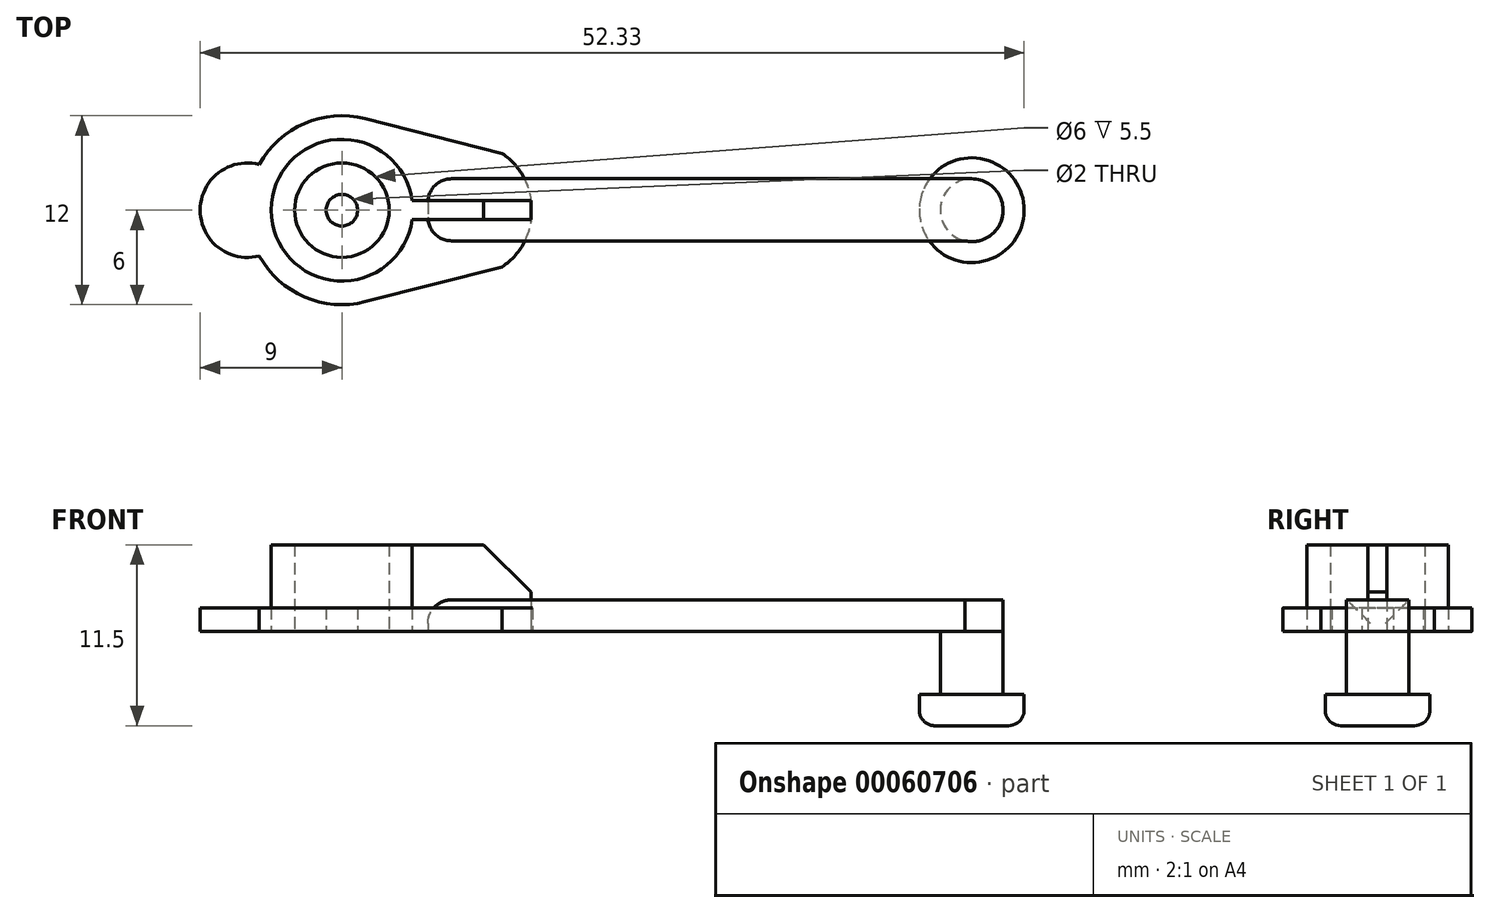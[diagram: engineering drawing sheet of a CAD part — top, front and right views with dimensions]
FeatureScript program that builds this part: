
annotation { "Feature Type Name" : "Feature", "Feature Type Description" : "" }
export const myFeature = defineFeature(function(context is Context, id is Id, definition is map)
    precondition{}
    {
        {
            var Q0;
            Q0=qCreatedBy(makeId("Top.planeOp"),FACE);
            var sketch = newSketch(context, id + "F0", { "sketchPlane" : qUnion([Q0])});
            skCircle(sketch, "E0", {"center": v(0, 0) * mm, "radius": 3 * mm});
            skArc(sketch, "E1", {"start": v(4.46, 0.6) * mm, "mid": v(-4.5, 0) * mm, "end": v(4.46, -0.6) * mm});
            skLineSegment(sketch, "E2.rect.bottom", {"start": v(12, -0.6) * mm, "end": v(4.46, -0.6) * mm});
            skLineSegment(sketch, "E2.rect.top", {"start": v(12, 0.6) * mm, "end": v(4.46, 0.6) * mm});
            skLineSegment(sketch, "E2.rect.left", {"start": v(12, -0.6) * mm, "end": v(12, 0.6) * mm});
            skPoint(sketch, "E2.rect.middle", {"position": v(7.75, 0) * mm});
            skArc(sketch, "E3", {"start": v(1.48, 5.81) * mm, "mid": v(-2.38, 5.5) * mm, "end": v(-5.25, 2.9) * mm});
            skArc(sketch, "E4", {"start": v(10.18, -3.6) * mm, "mid": v(12.1, 0) * mm, "end": v(10.18, 3.6) * mm});
            skLineSegment(sketch, "E5", {"start": v(7.33, -4.32) * mm, "end": v(1.48, -5.81) * mm});
            skLineSegment(sketch, "E6", {"start": v(7.33, 4.32) * mm, "end": v(1.48, 5.81) * mm});
            skPoint(sketch, "E7.orphan", {"position": v(10.18, 3.6) * mm});
            skPoint(sketch, "E8.orphan", {"position": v(10.18, -3.6) * mm});
            skLineSegment(sketch, "E9", {"start": v(7.33, 4.32) * mm, "end": v(10.18, 3.6) * mm});
            skLineSegment(sketch, "E10", {"start": v(10.18, -3.6) * mm, "end": v(7.33, -4.32) * mm});
            skCircle(sketch, "E11", {"center": v(0, 0) * mm, "radius": 1 * mm});
            skArc(sketch, "E12", {"start": v(-5.25, 2.9) * mm, "mid": v(-9, 0) * mm, "end": v(-5.25, -2.9) * mm});
            skArc(sketch, "E13.trimOffspring", {"start": v(-5.25, -2.9) * mm, "mid": v(-2.38, -5.5) * mm, "end": v(1.48, -5.81) * mm});
            skSolve(sketch);
        }
        {
            var Q0;
            {var subQ2=sQuery(id+"F0.wireOp",EDGE,"E1");Q0=makeQuery(id+"F0.imprint","IMPRINT",FACE,{"disambiguationData":[TD([[makeQuery(id+"F0.imprint","IMPRINT",EDGE,{"derivedFrom":subQ2}),-1.0]])]});}
            var Q1;
            Q1=makeQuery(id+"F0.imprint","IMPRINT",FACE,{"disambiguationData":[TD([[makeQuery(id+"F0.imprint","IMPRINT",EDGE,{"derivedFrom":sQuery(id+"F0.wireOp",EDGE,"E0")}),-1.0]])]});
            var Q2;
            {var subQ1=sQuery(id+"F0.wireOp",EDGE,"E2.rect.bottom");Q2=makeQuery(id+"F0.imprint","IMPRINT",FACE,{"disambiguationData":[TD([[makeQuery(id+"F0.imprint","IMPRINT",EDGE,{"derivedFrom":subQ1}),-1.0]])]});}
            var Q3;
            Q3=makeQuery(id+"F0.imprint","IMPRINT",FACE,{"disambiguationData":[TD([[makeQuery(id+"F0.imprint","IMPRINT",EDGE,{"derivedFrom":sQuery(id+"F0.wireOp",EDGE,"E0")}),1.0]])]});
            extrude(context, id + "F1", {"entities" : qUnion([Q0, Q1, Q2, Q3]), "depth" : 1.5 * mm});
        }
        {
            var Q0;
            Q0=makeQuery(id+"F0.imprint","IMPRINT",FACE,{"disambiguationData":[TD([[makeQuery(id+"F0.imprint","IMPRINT",EDGE,{"derivedFrom":sQuery(id+"F0.wireOp",EDGE,"E0")}),-1.0]])]});
            var Q1;
            {var subQ1=sQuery(id+"F0.wireOp",EDGE,"E2.rect.bottom");Q1=makeQuery(id+"F0.imprint","IMPRINT",FACE,{"disambiguationData":[TD([[makeQuery(id+"F0.imprint","IMPRINT",EDGE,{"derivedFrom":subQ1}),-1.0]])]});}
            extrude(context, id + "F2", {"entities" : qUnion([Q0, Q1]), "depth" : 5.5 * mm});
        }
        {
            var Q0;
            Q0=makeQuery(id+"F2.opExtrude","CAP_EDGE",EDGE,{"disambiguationData":[OSD([sQuery(id+"F0.wireOp",EDGE,"E2.rect.left")])],"isStart":false});
            chamfer(context, id + "F3", {"entities" : qUnion([Q0]), "chamferType" : ChamferType.OFFSET_ANGLE, "width" : 3 * mm, "oppositeDirection" : false, "angle" : 45 * degree});
        }
        {
            var Q0;
            {var subQ2=sQuery(id+"F0.wireOp",EDGE,"E1");Q0=makeQuery(id+"F0.imprint","IMPRINT",FACE,{"disambiguationData":[TD([[makeQuery(id+"F0.imprint","IMPRINT",EDGE,{"derivedFrom":subQ2}),-1.0]])]});}
            var sketch = newSketch(context, id + "F4", { "sketchPlane" : qUnion([Q0])});
            skCircle(sketch, "E14", {"center": v(40, 0) * mm, "radius": 2 * mm});
            skLineSegment(sketch, "E15.bottom", {"start": v(40, 2) * mm, "end": v(5.46, 2) * mm});
            skLineSegment(sketch, "E15.top", {"start": v(40, -1.95) * mm, "end": v(5.46, -1.95) * mm});
            skLineSegment(sketch, "E15.left", {"start": v(40, 2) * mm, "end": v(40, -1.95) * mm});
            skLineSegment(sketch, "E15.right", {"start": v(5.46, 2) * mm, "end": v(5.46, -1.95) * mm});
            skSolve(sketch);
        }
        {
            var Q0;
            {var subQ0=sQuery(id+"F4.wireOp",EDGE,"E15.left");Q0=makeQuery(id+"F4.imprint","IMPRINT",FACE,{"disambiguationData":[TD([[makeQuery(id+"F4.imprint","IMPRINT",EDGE,{"derivedFrom":subQ0}),1.0]])]});}
            var Q1;
            {var subQ0=sQuery(id+"F4.wireOp",EDGE,"E15.left");Q1=makeQuery(id+"F4.imprint","IMPRINT",FACE,{"disambiguationData":[TD([[makeQuery(id+"F4.imprint","IMPRINT",EDGE,{"derivedFrom":subQ0}),-1.0]])]});}
            extrude(context, id + "F5", {"entities" : qUnion([Q0, Q1]), "oppositeDirection" : true, "depth" : 4 * mm});
        }
        {
            var Q0;
            {var subQ1=sQuery(id+"F4.wireOp",EDGE,"E14");var subQ3=sQuery(id+"F4.wireOp",EDGE,"E15.top");var subQ4=makeQuery(id+"F4.imprint","INTERSECT",VERTEX,{"derivedFrom":[subQ1,subQ3]});Q0=makeQuery(id+"F4.imprint","IMPRINT",FACE,{"disambiguationData":[TD([[makeQuery(id+"F4.imprint","IMPRINT",EDGE,{"disambiguationData":[TD([[subQ4,-1.0]])],"derivedFrom":subQ3}),-1.0]])]});}
            var Q1;
            {var subQ5=makeQuery(id+"F0.imprint","IMPRINT",EDGE,{"derivedFrom":sQuery(id+"F0.wireOp",EDGE,"E2.rect.left")});Q1=makeQuery(id+"F4.imprint","IMPRINT",FACE,{"disambiguationData":[TD([[makeQuery(id+"F4.imprint","IMPRINT",EDGE,{"derivedFrom":subQ5}),1.0]])]});}
            var Q2;
            {var subQ5=makeQuery(id+"F0.imprint","IMPRINT",EDGE,{"derivedFrom":sQuery(id+"F0.wireOp",EDGE,"E2.rect.left")});Q2=makeQuery(id+"F4.imprint","IMPRINT",FACE,{"disambiguationData":[TD([[makeQuery(id+"F4.imprint","IMPRINT",EDGE,{"derivedFrom":subQ5}),-1.0]])]});}
            var Q3;
            {var subQ0=sQuery(id+"F4.wireOp",EDGE,"E15.left");Q3=makeQuery(id+"F4.imprint","IMPRINT",FACE,{"disambiguationData":[TD([[makeQuery(id+"F4.imprint","IMPRINT",EDGE,{"derivedFrom":subQ0}),-1.0]])]});}
            var Q4;
            {var subQ0=sQuery(id+"F4.wireOp",EDGE,"E15.left");Q4=makeQuery(id+"F4.imprint","IMPRINT",FACE,{"disambiguationData":[TD([[makeQuery(id+"F4.imprint","IMPRINT",EDGE,{"derivedFrom":subQ0}),1.0]])]});}
            extrude(context, id + "F6", {"entities" : qUnion([Q0, Q1, Q2, Q3, Q4]), "depth" : 2 * mm});
        }
        {
            var Q0;
            Q0=makeQuery(id+"F6.opExtrude","CAP_EDGE",EDGE,{"disambiguationData":[OSD([sQuery(id+"F4.wireOp",EDGE,"E15.right")])],"isStart":false});
            var Q1;
            Q1=makeQuery(id+"F6.opExtrude","SWEPT_EDGE",EDGE,{"disambiguationData":[OSD([sQuery(id+"F4.wireOp",EDGE,"E15.bottom"),sQuery(id+"F4.wireOp",EDGE,"E15.right")])]});
            var Q2;
            Q2=makeQuery(id+"F6.opExtrude","SWEPT_EDGE",EDGE,{"disambiguationData":[OSD([sQuery(id+"F4.wireOp",EDGE,"E15.top"),sQuery(id+"F4.wireOp",EDGE,"E15.right")])]});
            fillet(context, id + "F7", {"entities" : qUnion([Q0, Q1, Q2]), "radius" : 1.5 * mm, "tangentPropagation" : true, "allowEdgeOverflow" : false});
        }
        {
            var Q0;
            Q0=makeQuery(id+"F5.opExtrude","CAP_FACE",FACE,{"disambiguationData":[OSD([sQuery(id+"F4.wireOp",EDGE,"E14")])],"isStart":false});
            var sketch = newSketch(context, id + "F8", { "sketchPlane" : qUnion([Q0])});
            skCircle(sketch, "E16", {"center": v(40, 0) * mm, "radius": 3.33 * mm});
            skSolve(sketch);
        }
        {
            var Q0;
            Q0=makeQuery(id+"F8.imprint","IMPRINT",FACE,{"disambiguationData":[TD([[makeQuery(id+"F8.imprint","IMPRINT",EDGE,{"derivedFrom":sQuery(id+"F8.wireOp",EDGE,"E16")}),1.0]])]});
            var Q1;
            Q1=makeQuery(id+"F8.imprint","IMPRINT",FACE,{"disambiguationData":[TD([[makeQuery(id+"F8.imprint","IMPRINT",EDGE,{"derivedFrom":makeQuery(id+"F5.opExtrude","CAP_EDGE",EDGE,{"disambiguationData":[OSD([sQuery(id+"F4.wireOp",EDGE,"E14")])],"isStart":false})}),-1.0]])]});
            extrude(context, id + "F9", {"entities" : qUnion([Q0, Q1]), "operationType" : NewBodyOperationType.ADD, "depth" : 2 * mm});
        }
        {
            var Q0;
            Q0=makeQuery(id+"F9.opExtrude","CAP_EDGE",EDGE,{"disambiguationData":[OSD([sQuery(id+"F8.wireOp",EDGE,"E16")])],"isStart":false});
            fillet(context, id + "F10", {"entities" : qUnion([Q0]), "radius" : 1 * mm, "tangentPropagation" : true, "allowEdgeOverflow" : false});
        }
    });
